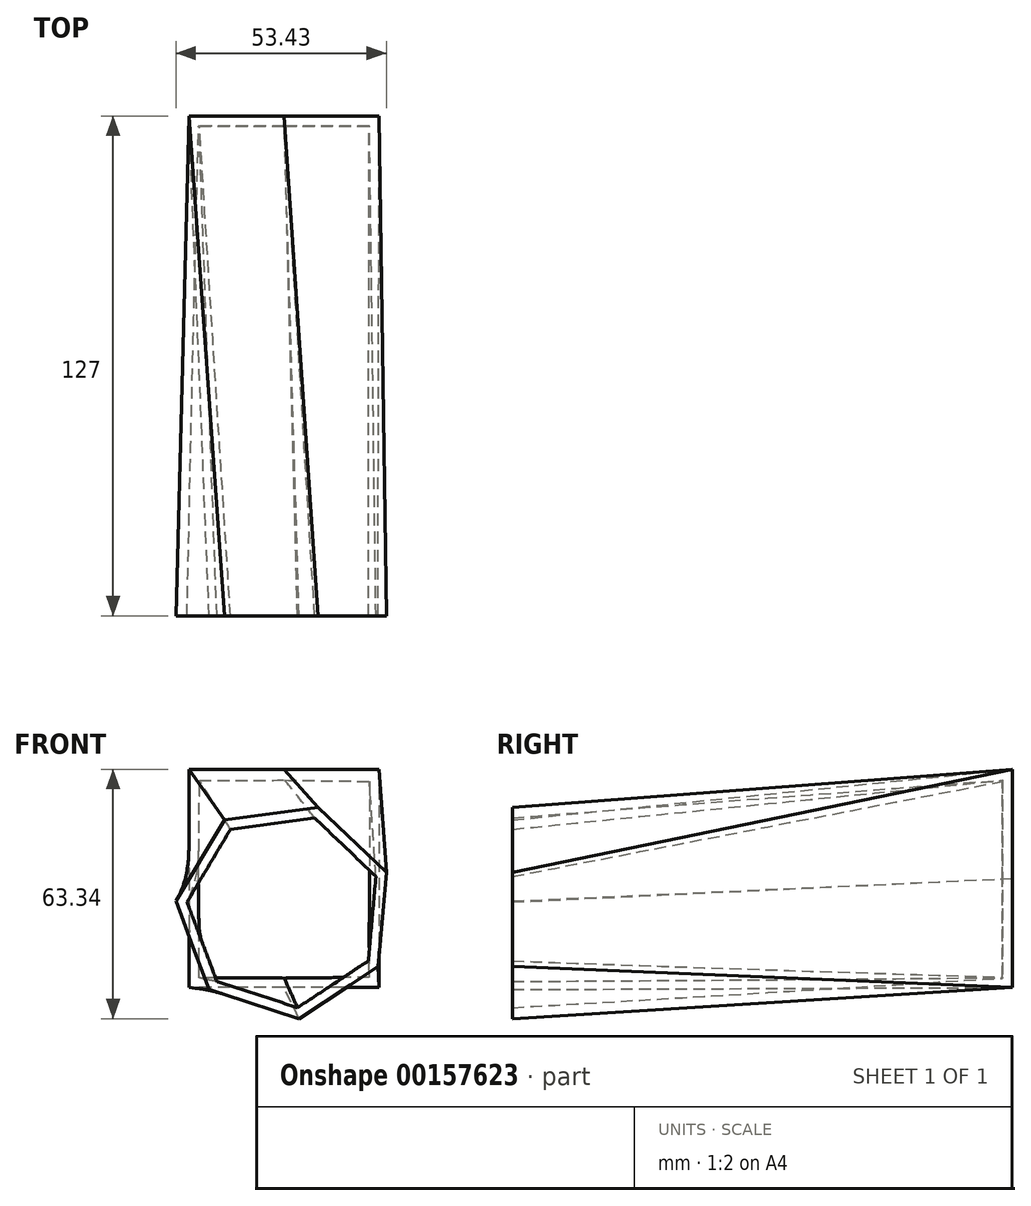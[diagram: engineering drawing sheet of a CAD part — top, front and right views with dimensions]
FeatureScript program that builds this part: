
annotation { "Feature Type Name" : "Feature", "Feature Type Description" : "" }
export const myFeature = defineFeature(function(context is Context, id is Id, definition is map)
    precondition{}
    {
        {
            var Q0;
            Q0=qCreatedBy(makeId("Front.planeOp"),FACE);
            var sketch = newSketch(context, id + "F0", { "sketchPlane" : qUnion([Q0])});
            skLineSegment(sketch, "E0.bottom", {"start": v(24.1, 35.94) * mm, "end": v(-24.29, 35.94) * mm});
            skLineSegment(sketch, "E0.top", {"start": v(24.1, -19.49) * mm, "end": v(-24.29, -19.49) * mm});
            skLineSegment(sketch, "E0.left", {"start": v(24.1, 35.94) * mm, "end": v(24.1, -19.49) * mm});
            skLineSegment(sketch, "E0.right", {"start": v(-24.29, 35.94) * mm, "end": v(-24.29, -19.49) * mm});
            skSolve(sketch);
        }
        {
            var Q0;
            Q0=qCreatedBy(makeId("Front.planeOp"),FACE);
            cPlane(context, id + "F1", {"entities" : qUnion([Q0]), "cplaneType" : CPlaneType.OFFSET, "offset" : 127 * mm, "width" : 152.4 * mm, "height" : 152.4 * mm});
        }
        {
            var Q0;
            Q0=qCreatedBy(id+"F1.planeOp",FACE);
            var sketch = newSketch(context, id + "F2", { "sketchPlane" : qUnion([Q0])});
            skCircle(sketch, "E1.cCircle", {"center": v(0, 0) * mm, "radius": 24.92 * mm, "construction": true});
            skLineSegment(sketch, "E1.0", {"start": v(-15.24, 23.08) * mm, "end": v(8.54, 26.3) * mm});
            skLineSegment(sketch, "E1.1", {"start": v(8.54, 26.3) * mm, "end": v(25.89, 9.73) * mm});
            skLineSegment(sketch, "E1.2", {"start": v(25.89, 9.73) * mm, "end": v(23.75, -14.18) * mm});
            skLineSegment(sketch, "E1.3", {"start": v(23.75, -14.18) * mm, "end": v(3.72, -27.4) * mm});
            skLineSegment(sketch, "E1.4", {"start": v(3.72, -27.4) * mm, "end": v(-19.1, -20) * mm});
            skLineSegment(sketch, "E1.5", {"start": v(-19.1, -20) * mm, "end": v(-27.54, 2.47) * mm});
            skLineSegment(sketch, "E1.6", {"start": v(-27.54, 2.47) * mm, "end": v(-15.24, 23.08) * mm});
            skPoint(sketch, "E1.0.midPoint", {"position": v(-3.35, 24.69) * mm});
            skSolve(sketch);
        }
        {
            var Q0;
            Q0=makeQuery(id+"F2.imprint","IMPRINT",FACE,{"disambiguationData":[TD([[makeQuery(id+"F2.imprint","IMPRINT",EDGE,{"derivedFrom":sQuery(id+"F2.wireOp",EDGE,"E1.0")}),-1.0]])]});
            var Q1;
            Q1=makeQuery(id+"F0.imprint","IMPRINT",FACE,{"disambiguationData":[TD([[makeQuery(id+"F0.imprint","IMPRINT",EDGE,{"derivedFrom":sQuery(id+"F0.wireOp",EDGE,"E0.bottom")}),1.0]])]});
            loft(context, id + "F3", {"sheetProfilesArray" : [{ "sheetProfileEntities" : qUnion([Q0]) }, { "sheetProfileEntities" : qUnion([Q1]) }]});
        }
        {
            var Q0;
            Q0=makeQuery(id+"F3.opLoft","CAP_FACE",FACE,{"disambiguationData":[OSD([makeQuery(id+"F2.imprint","IMPRINT",FACE,{"disambiguationData":[TD([[makeQuery(id+"F2.imprint","IMPRINT",EDGE,{"derivedFrom":sQuery(id+"F2.wireOp",EDGE,"E1.0")}),-1.0]])]})])],"isStart":true});
            shell(context, id + "F4", {"entities" : qUnion([Q0]), "thickness" : 2.54 * mm});
        }
    });
